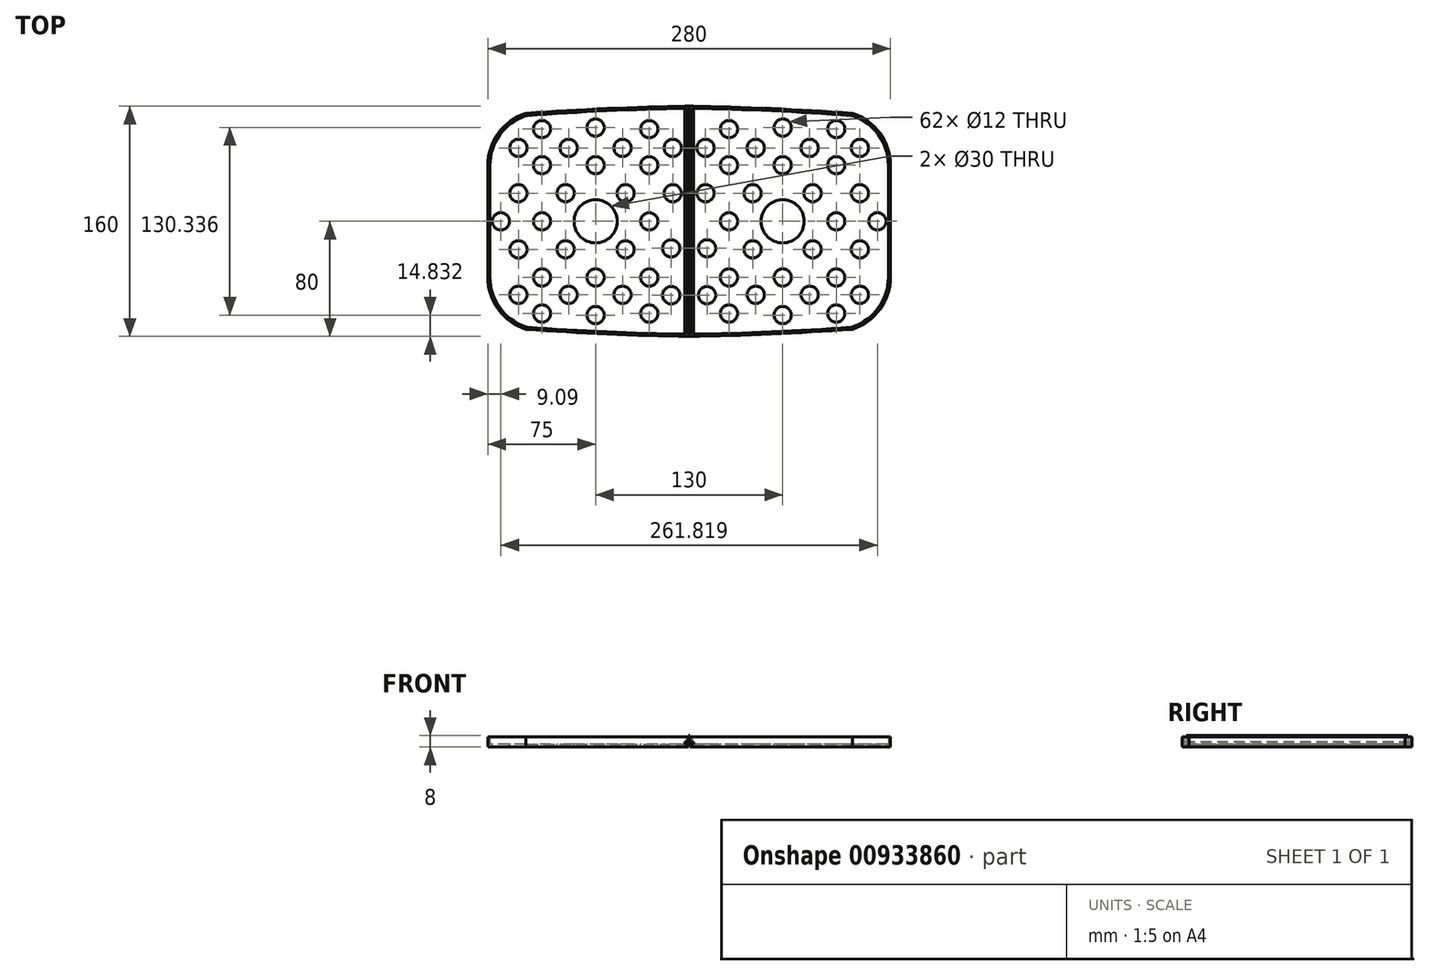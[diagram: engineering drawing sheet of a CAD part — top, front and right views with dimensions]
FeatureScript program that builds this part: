
annotation { "Feature Type Name" : "Feature", "Feature Type Description" : "" }
export const myFeature = defineFeature(function(context is Context, id is Id, definition is map)
    precondition{}
    {
        {
            var Q0;
            Q0=qCreatedBy(makeId("Top.planeOp"),FACE);
            var sketch = newSketch(context, id + "F0", { "sketchPlane" : qUnion([Q0])});
            skPoint(sketch, "E0.middle", {"position": v(0, 0) * mm});
            skLineSegment(sketch, "E1", {"start": v(0, 0) * mm, "end": v(140, 0) * mm, "construction": true});
            skLineSegment(sketch, "E2", {"start": v(0, 0) * mm, "end": v(0, 75) * mm, "construction": true});
            skLineSegment(sketch, "E3", {"start": v(140, -11.05) * mm, "end": v(65, -11.05) * mm, "construction": true});
            skLineSegment(sketch, "E4", {"start": v(65, 0) * mm, "end": v(65, 78) * mm, "construction": true});
            skPoint(sketch, "E5.visualSharp", {"position": v(140, 75) * mm});
            skLineSegment(sketch, "E6.MirrorCS", {"start": v(0, 0) * mm, "end": v(0, -75) * mm, "construction": true});
            skCircle(sketch, "E7", {"center": v(65, 0) * mm, "radius": 15 * mm});
            skLineSegment(sketch, "E8", {"start": v(65, 39) * mm, "end": v(139.51, 39) * mm, "construction": true});
            skLineSegment(sketch, "E9", {"start": v(102.26, 39) * mm, "end": v(102.26, 72.53) * mm, "construction": true});
            skPoint(sketch, "E10.startSnap0", {"position": v(102.26, 55.76) * mm});
            skLineSegment(sketch, "E11", {"start": v(102.26, 39) * mm, "end": v(102.26, 0) * mm, "construction": true});
            skLineSegment(sketch, "E12", {"start": v(140, 19.5) * mm, "end": v(65, 19.5) * mm, "construction": true});
            skPoint(sketch, "E12.startSnap0", {"position": v(102.26, 19.5) * mm});
            skCircle(sketch, "E13", {"center": v(65, 39) * mm, "radius": 6 * mm});
            skCircle(sketch, "E14", {"center": v(85.86, 19.5) * mm, "radius": 6 * mm});
            skCircle(sketch, "E15", {"center": v(83.75, 51.05) * mm, "radius": 6 * mm});
            skCircle(sketch, "E16", {"center": v(65, 65.17) * mm, "radius": 6 * mm});
            skCircle(sketch, "E17", {"center": v(102.26, 64.08) * mm, "radius": 6 * mm});
            skCircle(sketch, "E18", {"center": v(102.26, 39) * mm, "radius": 6 * mm});
            skCircle(sketch, "E19", {"center": v(102.26, 0) * mm, "radius": 6 * mm});
            skCircle(sketch, "E20", {"center": v(118.66, 51.05) * mm, "radius": 6 * mm});
            skCircle(sketch, "E21", {"center": v(118.66, 19.5) * mm, "radius": 6 * mm});
            skCircle(sketch, "E22", {"center": v(130.9, 0) * mm, "radius": 6 * mm});
            skCircle(sketch, "E23.MirrorC", {"center": v(46.25, 51.05) * mm, "radius": 6 * mm});
            skCircle(sketch, "E24.MirrorC", {"center": v(27.74, 64.08) * mm, "radius": 6 * mm});
            skCircle(sketch, "E25.MirrorC", {"center": v(11.34, 51.05) * mm, "radius": 6 * mm});
            skCircle(sketch, "E26.MirrorC", {"center": v(27.74, 39) * mm, "radius": 6 * mm});
            skCircle(sketch, "E27.MirrorC", {"center": v(44.14, 19.5) * mm, "radius": 6 * mm});
            skCircle(sketch, "E28.MirrorC", {"center": v(27.74, 0) * mm, "radius": 6 * mm});
            skCircle(sketch, "E29.MirrorC", {"center": v(11.34, 19.5) * mm, "radius": 6 * mm});
            skCircle(sketch, "E30.MirrorC", {"center": v(12.5, -18.79) * mm, "radius": 6 * mm});
            skCircle(sketch, "E31.MirrorC", {"center": v(12.5, -51.34) * mm, "radius": 6 * mm});
            skCircle(sketch, "E32.MirrorC", {"center": v(27.74, -64.08) * mm, "radius": 6 * mm});
            skCircle(sketch, "E33.MirrorC", {"center": v(27.74, -39) * mm, "radius": 6 * mm});
            skCircle(sketch, "E34.MirrorC", {"center": v(46.25, -51.05) * mm, "radius": 6 * mm});
            skCircle(sketch, "E35.MirrorC", {"center": v(44.14, -19.5) * mm, "radius": 6 * mm});
            skCircle(sketch, "E36.MirrorC", {"center": v(65, -39) * mm, "radius": 6 * mm});
            skCircle(sketch, "E37.MirrorC", {"center": v(65, -65.17) * mm, "radius": 6 * mm});
            skCircle(sketch, "E38.MirrorC", {"center": v(83.75, -51.05) * mm, "radius": 6 * mm});
            skCircle(sketch, "E39.MirrorC", {"center": v(85.86, -19.5) * mm, "radius": 6 * mm});
            skCircle(sketch, "E40.MirrorC", {"center": v(102.26, -39) * mm, "radius": 6 * mm});
            skCircle(sketch, "E41.MirrorC", {"center": v(102.26, -64.08) * mm, "radius": 6 * mm});
            skCircle(sketch, "E42.MirrorC", {"center": v(118.66, -51.05) * mm, "radius": 6 * mm});
            skCircle(sketch, "E43.MirrorC", {"center": v(118.66, -19.5) * mm, "radius": 6 * mm});
            skLineSegment(sketch, "E44.trimOffspring", {"start": v(2.25, -75.01) * mm, "end": v(2.25, -75.02) * mm});
            skLineSegment(sketch, "E45.trimOffspring", {"start": v(0.5, 80) * mm, "end": v(0.5, 80) * mm});
            skLineSegment(sketch, "E46", {"start": v(140, 0) * mm, "end": v(140, 38.77) * mm});
            skLineSegment(sketch, "E47", {"start": v(0.5, 80) * mm, "end": v(0.5, 0) * mm});
            skArc(sketch, "E48.filletArc", {"start": v(140, 38.77) * mm, "mid": v(132.65, 61.23) * mm, "end": v(113.45, 75) * mm});
            skLineSegment(sketch, "E49.MirrorCS", {"start": v(0.5, -80) * mm, "end": v(0.5, 0) * mm});
            skArc(sketch, "E50.MirrorCS", {"start": v(140, -38.77) * mm, "mid": v(132.65, -61.23) * mm, "end": v(113.45, -75) * mm});
            skLineSegment(sketch, "E51.MirrorCS", {"start": v(140, 0) * mm, "end": v(140, -38.77) * mm});
            skArc(sketch, "E52.1", {"start": v(138.5, 38.77) * mm, "mid": v(131.68, 60) * mm, "end": v(113.78, 73.31) * mm});
            skLineSegment(sketch, "E52.2", {"start": v(2, 78.48) * mm, "end": v(2, 0.25) * mm});
            skLineSegment(sketch, "E52.3", {"start": v(138.5, 0) * mm, "end": v(138.5, 38.77) * mm});
            skLineSegment(sketch, "E52.4", {"start": v(2, -78.44) * mm, "end": v(2, 0.25) * mm});
            skArc(sketch, "E52.6", {"start": v(138.5, -38.77) * mm, "mid": v(131.69, -60) * mm, "end": v(113.8, -73.3) * mm});
            skLineSegment(sketch, "E52.7", {"start": v(138.5, 0) * mm, "end": v(138.5, -38.77) * mm});
            skLineSegment(sketch, "E53.MirrorCS", {"start": v(-0.5, 80) * mm, "end": v(-0.5, 0) * mm});
            skArc(sketch, "E54.MirrorCS", {"start": v(-140, 38.77) * mm, "mid": v(-132.65, 61.23) * mm, "end": v(-113.45, 75) * mm});
            skLineSegment(sketch, "E55.MirrorCS", {"start": v(-140, 0) * mm, "end": v(-140, 38.77) * mm});
            skLineSegment(sketch, "E56.MirrorCS", {"start": v(-140, 0) * mm, "end": v(-140, -38.77) * mm});
            skArc(sketch, "E57.MirrorCS", {"start": v(-140, -38.77) * mm, "mid": v(-132.65, -61.23) * mm, "end": v(-113.45, -75) * mm});
            skLineSegment(sketch, "E58.MirrorCS", {"start": v(-0.5, -80) * mm, "end": v(-0.5, 0) * mm});
            skCircle(sketch, "E59.MirrorC", {"center": v(-11.34, 51.05) * mm, "radius": 6 * mm});
            skCircle(sketch, "E60.MirrorC", {"center": v(-27.74, 64.08) * mm, "radius": 6 * mm});
            skCircle(sketch, "E61.MirrorC", {"center": v(-46.25, 51.05) * mm, "radius": 6 * mm});
            skCircle(sketch, "E62.MirrorC", {"center": v(-65, 65.17) * mm, "radius": 6 * mm});
            skCircle(sketch, "E63.MirrorC", {"center": v(-27.74, 39) * mm, "radius": 6 * mm});
            skCircle(sketch, "E64.MirrorC", {"center": v(-11.34, 19.5) * mm, "radius": 6 * mm});
            skCircle(sketch, "E65.MirrorC", {"center": v(-44.14, 19.5) * mm, "radius": 6 * mm});
            skCircle(sketch, "E66.MirrorC", {"center": v(-65, 39) * mm, "radius": 6 * mm});
            skCircle(sketch, "E67.MirrorC", {"center": v(-65, 0) * mm, "radius": 15 * mm});
            skCircle(sketch, "E68.MirrorC", {"center": v(-27.74, 0) * mm, "radius": 6 * mm});
            skCircle(sketch, "E69.MirrorC", {"center": v(-12.5, -18.79) * mm, "radius": 6 * mm});
            skCircle(sketch, "E70.MirrorC", {"center": v(-44.14, -19.5) * mm, "radius": 6 * mm});
            skCircle(sketch, "E71.MirrorC", {"center": v(-27.74, -39) * mm, "radius": 6 * mm});
            skCircle(sketch, "E72.MirrorC", {"center": v(-12.5, -51.34) * mm, "radius": 6 * mm});
            skCircle(sketch, "E73.MirrorC", {"center": v(-27.74, -64.08) * mm, "radius": 6 * mm});
            skCircle(sketch, "E74.MirrorC", {"center": v(-46.25, -51.05) * mm, "radius": 6 * mm});
            skCircle(sketch, "E75.MirrorC", {"center": v(-65, -65.17) * mm, "radius": 6 * mm});
            skCircle(sketch, "E76.MirrorC", {"center": v(-65, -39) * mm, "radius": 6 * mm});
            skCircle(sketch, "E77.MirrorC", {"center": v(-83.75, -51.05) * mm, "radius": 6 * mm});
            skCircle(sketch, "E78.MirrorC", {"center": v(-102.26, -64.08) * mm, "radius": 6 * mm});
            skCircle(sketch, "E79.MirrorC", {"center": v(-118.66, -51.05) * mm, "radius": 6 * mm});
            skCircle(sketch, "E80.MirrorC", {"center": v(-102.26, -39) * mm, "radius": 6 * mm});
            skCircle(sketch, "E81.MirrorC", {"center": v(-118.66, -19.5) * mm, "radius": 6 * mm});
            skCircle(sketch, "E82.MirrorC", {"center": v(-85.86, -19.5) * mm, "radius": 6 * mm});
            skCircle(sketch, "E83.MirrorC", {"center": v(-102.26, 0) * mm, "radius": 6 * mm});
            skCircle(sketch, "E84.MirrorC", {"center": v(-130.9, 0) * mm, "radius": 6 * mm});
            skCircle(sketch, "E85.MirrorC", {"center": v(-85.86, 19.5) * mm, "radius": 6 * mm});
            skCircle(sketch, "E86.MirrorC", {"center": v(-118.66, 19.5) * mm, "radius": 6 * mm});
            skCircle(sketch, "E87.MirrorC", {"center": v(-83.75, 51.05) * mm, "radius": 6 * mm});
            skCircle(sketch, "E88.MirrorC", {"center": v(-102.26, 39) * mm, "radius": 6 * mm});
            skCircle(sketch, "E89.MirrorC", {"center": v(-102.26, 64.08) * mm, "radius": 6 * mm});
            skCircle(sketch, "E90.MirrorC", {"center": v(-118.66, 51.05) * mm, "radius": 6 * mm});
            skArc(sketch, "E91.1", {"start": v(-138.5, 38.77) * mm, "mid": v(-131.69, 60) * mm, "end": v(-113.8, 73.3) * mm});
            skLineSegment(sketch, "E91.2", {"start": v(-2, 78.44) * mm, "end": v(-2, 0.25) * mm});
            skLineSegment(sketch, "E91.3", {"start": v(-138.5, 0) * mm, "end": v(-138.5, 38.77) * mm});
            skLineSegment(sketch, "E91.4", {"start": v(-2, -78.44) * mm, "end": v(-2, 0.25) * mm});
            skArc(sketch, "E91.6", {"start": v(-138.5, -38.77) * mm, "mid": v(-131.69, -60) * mm, "end": v(-113.8, -73.3) * mm});
            skLineSegment(sketch, "E91.7", {"start": v(-138.5, 0) * mm, "end": v(-138.5, -38.77) * mm});
            skPoint(sketch, "E92.startDerivative.orphan", {"position": v(127.12, 75) * mm});
            skArc(sketch, "E93", {"start": v(113.45, 75) * mm, "mid": v(57.01, 78.37) * mm, "end": v(0.5, 80) * mm});
            skPoint(sketch, "E94.MirrorCS.end.orphan", {"position": v(-0.5, 80) * mm});
            skPoint(sketch, "E94.MirrorCS.start.orphan", {"position": v(-113.45, 75) * mm});
            skPoint(sketch, "E95.MirrorCS.end.orphan", {"position": v(-0.5, -80) * mm});
            skPoint(sketch, "E95.MirrorCS.start.orphan", {"position": v(-113.45, -75) * mm});
            skPoint(sketch, "E96.MirrorCS.end.orphan", {"position": v(0.5, -80) * mm});
            skPoint(sketch, "E96.MirrorCS.start.orphan", {"position": v(113.45, -75) * mm});
            skArc(sketch, "E97.0", {"start": v(112.56, 73.56) * mm, "mid": v(57.32, 76.86) * mm, "end": v(2, 78.48) * mm});
            skArc(sketch, "E98.trimOffspring", {"start": v(0.5, 78.5) * mm, "mid": v(0.49, 78.5) * mm, "end": v(0.48, 78.5) * mm});
            skArc(sketch, "E99.MirrorCS", {"start": v(112.55, -73.56) * mm, "mid": v(57.31, -76.86) * mm, "end": v(2, -78.48) * mm});
            skArc(sketch, "E100.MirrorCS", {"start": v(113.45, -75) * mm, "mid": v(57.01, -78.37) * mm, "end": v(0.5, -80) * mm});
            skArc(sketch, "E101.MirrorCS", {"start": v(-113.45, 75) * mm, "mid": v(-57.01, 78.37) * mm, "end": v(-0.5, 80) * mm});
            skArc(sketch, "E102.MirrorCS", {"start": v(-112.55, 73.56) * mm, "mid": v(-57.31, 76.86) * mm, "end": v(-2, 78.48) * mm});
            skArc(sketch, "E103.MirrorCS", {"start": v(-112.55, -73.56) * mm, "mid": v(-57.31, -76.86) * mm, "end": v(-2, -78.48) * mm});
            skArc(sketch, "E104.MirrorCS", {"start": v(-113.45, -75) * mm, "mid": v(-57.01, -78.37) * mm, "end": v(-0.5, -80) * mm});
            skLineSegment(sketch, "E105", {"start": v(113.34, 73.5) * mm, "end": v(113.12, 73.53) * mm});
            skLineSegment(sketch, "E106", {"start": v(113.12, -73.53) * mm, "end": v(113.34, -73.5) * mm});
            skLineSegment(sketch, "E107", {"start": v(-113.12, -73.53) * mm, "end": v(-113.34, -73.5) * mm});
            skLineSegment(sketch, "E108", {"start": v(-113.12, 73.53) * mm, "end": v(-113.34, 73.5) * mm});
            skLineSegment(sketch, "E109", {"start": v(2, -78.44) * mm, "end": v(2, -78.48) * mm});
            skLineSegment(sketch, "E110", {"start": v(-2, -78.48) * mm, "end": v(-2, -78.44) * mm});
            skLineSegment(sketch, "E111", {"start": v(-2, 78.44) * mm, "end": v(-2, 78.48) * mm});
            skPoint(sketch, "E112.newPointA", {"position": v(113.34, -73.5) * mm});
            skArc(sketch, "E112.filletArc", {"start": v(112.55, -73.56) * mm, "mid": v(113.18, -73.48) * mm, "end": v(113.8, -73.3) * mm});
            skPoint(sketch, "E113.newPointB", {"position": v(113.34, 73.5) * mm});
            skArc(sketch, "E113.filletArc", {"start": v(113.78, 73.31) * mm, "mid": v(113.18, 73.48) * mm, "end": v(112.56, 73.56) * mm});
            skPoint(sketch, "E114.newPointB", {"position": v(-113.34, 73.5) * mm});
            skArc(sketch, "E114.filletArc", {"start": v(-112.55, 73.56) * mm, "mid": v(-113.18, 73.48) * mm, "end": v(-113.8, 73.3) * mm});
            skPoint(sketch, "E115.newPointB", {"position": v(-113.34, -73.5) * mm});
            skArc(sketch, "E115.filletArc", {"start": v(-113.8, -73.3) * mm, "mid": v(-113.18, -73.48) * mm, "end": v(-112.55, -73.56) * mm});
            skSolve(sketch);
        }
        {
            var Q0;
            Q0=makeQuery(id+"F0.imprint","IMPRINT",FACE,{"disambiguationData":[TD([[makeQuery(id+"F0.imprint","IMPRINT",EDGE,{"derivedFrom":sQuery(id+"F0.wireOp",EDGE,"E59.MirrorC")}),-1.0]])]});
            var Q1;
            Q1=makeQuery(id+"F0.imprint","IMPRINT",FACE,{"disambiguationData":[TD([[makeQuery(id+"F0.imprint","IMPRINT",EDGE,{"derivedFrom":sQuery(id+"F0.wireOp",EDGE,"E7")}),-1.0]])]});
            var Q2;
            Q2=makeQuery(id+"F0.imprint","IMPRINT",FACE,{"disambiguationData":[TD([[makeQuery(id+"F0.imprint","IMPRINT",EDGE,{"derivedFrom":sQuery(id+"F0.wireOp",EDGE,"E46")}),1.0]])]});
            var Q3;
            Q3=makeQuery(id+"F0.imprint","IMPRINT",FACE,{"disambiguationData":[TD([[makeQuery(id+"F0.imprint","IMPRINT",EDGE,{"derivedFrom":sQuery(id+"F0.wireOp",EDGE,"E53.MirrorCS")}),-1.0]])]});
            extrude(context, id + "F1", {"entities" : qUnion([Q0, Q1, Q2, Q3]), "oppositeDirection" : true, "depth" : 2 * mm, "offsetDistance" : 25 * mm});
        }
        {
            var Q0;
            Q0=makeQuery(id+"F0.imprint","IMPRINT",FACE,{"disambiguationData":[TD([[makeQuery(id+"F0.imprint","IMPRINT",EDGE,{"derivedFrom":sQuery(id+"F0.wireOp",EDGE,"E46")}),1.0]])]});
            var Q1;
            Q1=makeQuery(id+"F0.imprint","IMPRINT",FACE,{"disambiguationData":[TD([[makeQuery(id+"F0.imprint","IMPRINT",EDGE,{"derivedFrom":sQuery(id+"F0.wireOp",EDGE,"E53.MirrorCS")}),-1.0]])]});
            extrude(context, id + "F2", {"entities" : qUnion([Q0, Q1]), "operationType" : NewBodyOperationType.ADD, "depth" : 5 * mm, "offsetDistance" : 25 * mm});
        }
        {
            var Q0;
            Q0=qCreatedBy(makeId("Top.planeOp"),FACE);
            var sketch = newSketch(context, id + "F3", { "sketchPlane" : qUnion([Q0])});
            skLineSegment(sketch, "E116.bottom", {"start": v(3, -80) * mm, "end": v(-3, -80) * mm});
            skLineSegment(sketch, "E116.top", {"start": v(3, 80) * mm, "end": v(-3, 80) * mm});
            skLineSegment(sketch, "E116.left", {"start": v(3, -80) * mm, "end": v(3, 80) * mm});
            skLineSegment(sketch, "E116.right", {"start": v(-3, -80) * mm, "end": v(-3, 80) * mm});
            skPoint(sketch, "E116.middle", {"position": v(0, 0) * mm});
            skLineSegment(sketch, "E117.0", {"start": v(3, 77) * mm, "end": v(-3, 77) * mm, "construction": true});
            skLineSegment(sketch, "E118.0", {"start": v(3, -77) * mm, "end": v(-3, -77) * mm, "construction": true});
            skLineSegment(sketch, "E119.bottom", {"start": v(0.5, -77) * mm, "end": v(-0.5, -77) * mm});
            skLineSegment(sketch, "E119.top", {"start": v(0.5, 77) * mm, "end": v(-0.5, 77) * mm});
            skLineSegment(sketch, "E119.left", {"start": v(0.5, -77) * mm, "end": v(0.5, 77) * mm});
            skLineSegment(sketch, "E119.right", {"start": v(-0.5, -77) * mm, "end": v(-0.5, 77) * mm});
            skSolve(sketch);
        }
        {
            var Q0;
            Q0=makeQuery(id+"F3.imprint","IMPRINT",FACE,{"disambiguationData":[TD([[makeQuery(id+"F3.imprint","IMPRINT",EDGE,{"derivedFrom":sQuery(id+"F3.wireOp",EDGE,"E116.bottom")}),-1.0]])]});
            var Q1;
            Q1=makeQuery(id+"F3.imprint","IMPRINT",FACE,{"disambiguationData":[TD([[makeQuery(id+"F3.imprint","IMPRINT",EDGE,{"derivedFrom":sQuery(id+"F3.wireOp",EDGE,"E119.bottom")}),-1.0]])]});
            extrude(context, id + "F4", {"entities" : qUnion([Q0, Q1]), "depth" : 1.5 * mm, "offsetDistance" : 25 * mm});
        }
        {
            var Q0;
            Q0=makeQuery(id+"F3.imprint","IMPRINT",FACE,{"disambiguationData":[TD([[makeQuery(id+"F3.imprint","IMPRINT",EDGE,{"derivedFrom":sQuery(id+"F3.wireOp",EDGE,"E119.bottom")}),-1.0]])]});
            extrude(context, id + "F5", {"entities" : qUnion([Q0]), "operationType" : NewBodyOperationType.ADD, "depth" : 6 * mm, "offsetDistance" : 25 * mm});
        }
    });
